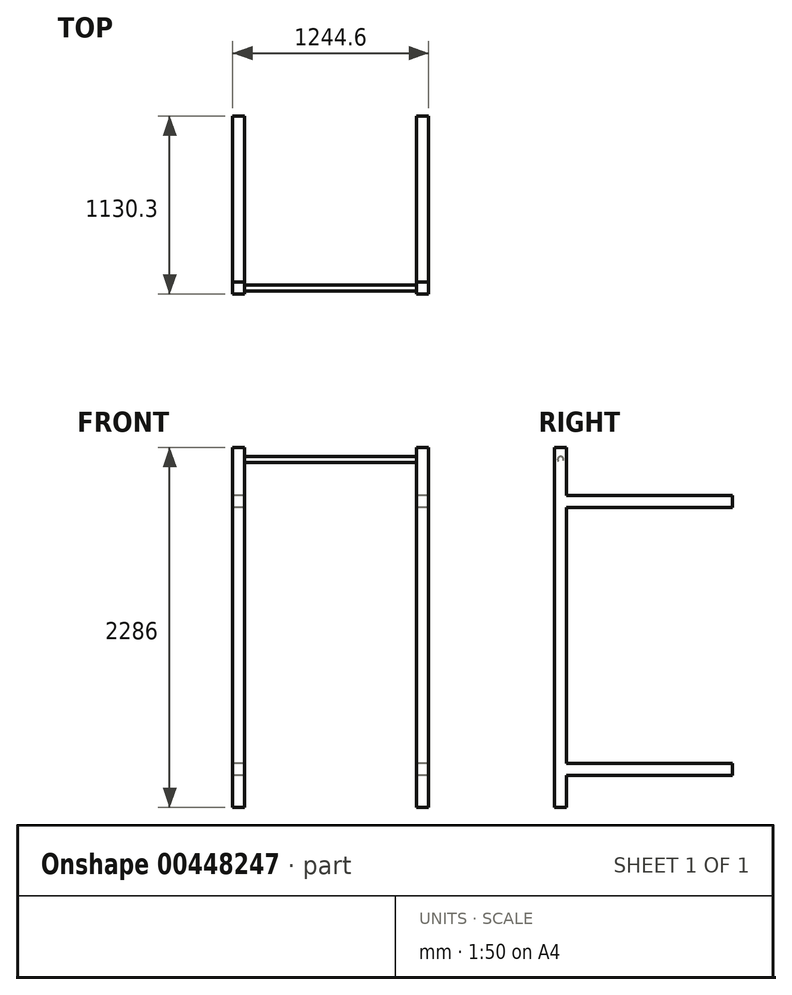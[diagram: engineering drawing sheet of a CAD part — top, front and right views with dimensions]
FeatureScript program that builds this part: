
annotation { "Feature Type Name" : "Feature", "Feature Type Description" : "" }
export const myFeature = defineFeature(function(context is Context, id is Id, definition is map)
    precondition{}
    {
        {
            var Q0;
            Q0=qCreatedBy(makeId("Top.planeOp"),FACE);
            var sketch = newSketch(context, id + "F0", { "sketchPlane" : qUnion([Q0])});
            skLineSegment(sketch, "E0.bottom", {"start": v(-622.3, -1054.1) * mm, "end": v(-546.1, -1054.1) * mm});
            skLineSegment(sketch, "E0.top", {"start": v(-622.3, -1130.3) * mm, "end": v(-546.1, -1130.3) * mm});
            skLineSegment(sketch, "E0.left", {"start": v(-622.3, -1054.1) * mm, "end": v(-622.3, -1130.3) * mm});
            skLineSegment(sketch, "E0.right", {"start": v(-546.1, -1054.1) * mm, "end": v(-546.1, -1130.3) * mm});
            skLineSegment(sketch, "E1.MirrorCS", {"start": v(622.3, -1054.1) * mm, "end": v(546.1, -1054.1) * mm});
            skLineSegment(sketch, "E2.MirrorCS", {"start": v(622.3, -1130.3) * mm, "end": v(546.1, -1130.3) * mm});
            skLineSegment(sketch, "E3.MirrorCS", {"start": v(546.1, -1054.1) * mm, "end": v(546.1, -1130.3) * mm});
            skLineSegment(sketch, "E4.MirrorCS", {"start": v(622.3, -1054.1) * mm, "end": v(622.3, -1130.3) * mm});
            skSolve(sketch);
        }
        {
            var Q0;
            Q0 = qSketchRegion(id + "F0", true);
            extrude(context, id + "F1", {"entities" : qUnion([Q0]), "depth" : 2286 * mm});
        }
        {
            var Q0;
            Q0=qCreatedBy(makeId("Front.planeOp"),FACE);
            var sketch = newSketch(context, id + "F2", { "sketchPlane" : qUnion([Q0])});
            skLineSegment(sketch, "E5.bottom", {"start": v(622.3, 1981.2) * mm, "end": v(546.1, 1981.2) * mm});
            skLineSegment(sketch, "E5.top", {"start": v(622.3, 1905) * mm, "end": v(546.1, 1905) * mm});
            skLineSegment(sketch, "E5.left", {"start": v(622.3, 1981.2) * mm, "end": v(622.3, 1905) * mm});
            skLineSegment(sketch, "E5.right", {"start": v(546.1, 1981.2) * mm, "end": v(546.1, 1905) * mm});
            skLineSegment(sketch, "E6.MirrorCS", {"start": v(-546.1, 1981.2) * mm, "end": v(-546.1, 1905) * mm});
            skLineSegment(sketch, "E7.MirrorCS", {"start": v(-622.3, 1981.2) * mm, "end": v(-622.3, 1905) * mm});
            skLineSegment(sketch, "E8.MirrorCS", {"start": v(-622.3, 1981.2) * mm, "end": v(-546.1, 1981.2) * mm});
            skLineSegment(sketch, "E9.MirrorCS", {"start": v(-622.3, 1905) * mm, "end": v(-546.1, 1905) * mm});
            skLineSegment(sketch, "E10", {"start": v(624.98, 1092.2) * mm, "end": v(-616.74, 1092.2) * mm, "construction": true});
            skLineSegment(sketch, "E11.MirrorCS", {"start": v(-622.3, 203.2) * mm, "end": v(-546.1, 203.2) * mm});
            skLineSegment(sketch, "E12.MirrorCS", {"start": v(-622.3, 203.2) * mm, "end": v(-622.3, 279.4) * mm});
            skLineSegment(sketch, "E13.MirrorCS", {"start": v(-546.1, 203.2) * mm, "end": v(-546.1, 279.4) * mm});
            skLineSegment(sketch, "E14.MirrorCS", {"start": v(546.1, 203.2) * mm, "end": v(546.1, 279.4) * mm});
            skLineSegment(sketch, "E15.MirrorCS", {"start": v(622.3, 203.2) * mm, "end": v(622.3, 279.4) * mm});
            skLineSegment(sketch, "E16.MirrorCS", {"start": v(622.3, 279.4) * mm, "end": v(546.1, 279.4) * mm});
            skLineSegment(sketch, "E17.MirrorCS", {"start": v(-622.3, 279.4) * mm, "end": v(-546.1, 279.4) * mm});
            skLineSegment(sketch, "E18.MirrorCS", {"start": v(622.3, 203.2) * mm, "end": v(546.1, 203.2) * mm});
            skSolve(sketch);
        }
        {
            var Q0;
            Q0 = qSketchRegion(id + "F2", true);
            extrude(context, id + "F3", {"entities" : qUnion([Q0]), "operationType" : NewBodyOperationType.ADD, "endBound" : BoundingType.UP_TO_NEXT, "depth" : 25.4 * mm});
        }
        {
            var Q0;
            Q0=makeQuery(id+"F3.boolean.opBoolean","MERGE",FACE,{"derivedFrom":[makeQuery(id+"F1.opExtrude","SWEPT_FACE",FACE,{"disambiguationData":[OSD([sQuery(id+"F0.wireOp",EDGE,"E0.right")])]}),makeQuery(id+"F3.opExtrude","SWEPT_FACE",FACE,{"disambiguationData":[OSD([sQuery(id+"F2.wireOp",EDGE,"E6.MirrorCS")])]}),makeQuery(id+"F3.opExtrude","SWEPT_FACE",FACE,{"disambiguationData":[OSD([sQuery(id+"F2.wireOp",EDGE,"E13.MirrorCS")])]})]});
            var sketch = newSketch(context, id + "F4", { "sketchPlane" : qUnion([Q0])});
            skCircle(sketch, "E19", {"center": v(-1092.2, 2209.8) * mm, "radius": 19.05 * mm});
            skLineSegment(sketch, "E20", {"start": v(-1092.2, 2286) * mm, "end": v(-1092.2, 2235.2) * mm, "construction": true});
            skSolve(sketch);
        }
        {
            var Q0;
            Q0 = qSketchRegion(id + "F4", true);
            var Q1;
            Q1=makeQuery(id+"F1.opExtrude","SWEPT_BODY",BODY,{"disambiguationData":[OSD([sQuery(id+"F0.wireOp",EDGE,"E1.MirrorCS"),sQuery(id+"F0.wireOp",EDGE,"E2.MirrorCS"),sQuery(id+"F0.wireOp",EDGE,"E3.MirrorCS"),sQuery(id+"F0.wireOp",EDGE,"E4.MirrorCS")])]});
            extrude(context, id + "F5", {"entities" : qUnion([Q0]), "endBound" : BoundingType.UP_TO_BODY, "endBoundEntityBody" : qUnion([Q1]), "depth" : 25.4 * mm});
        }
    });
